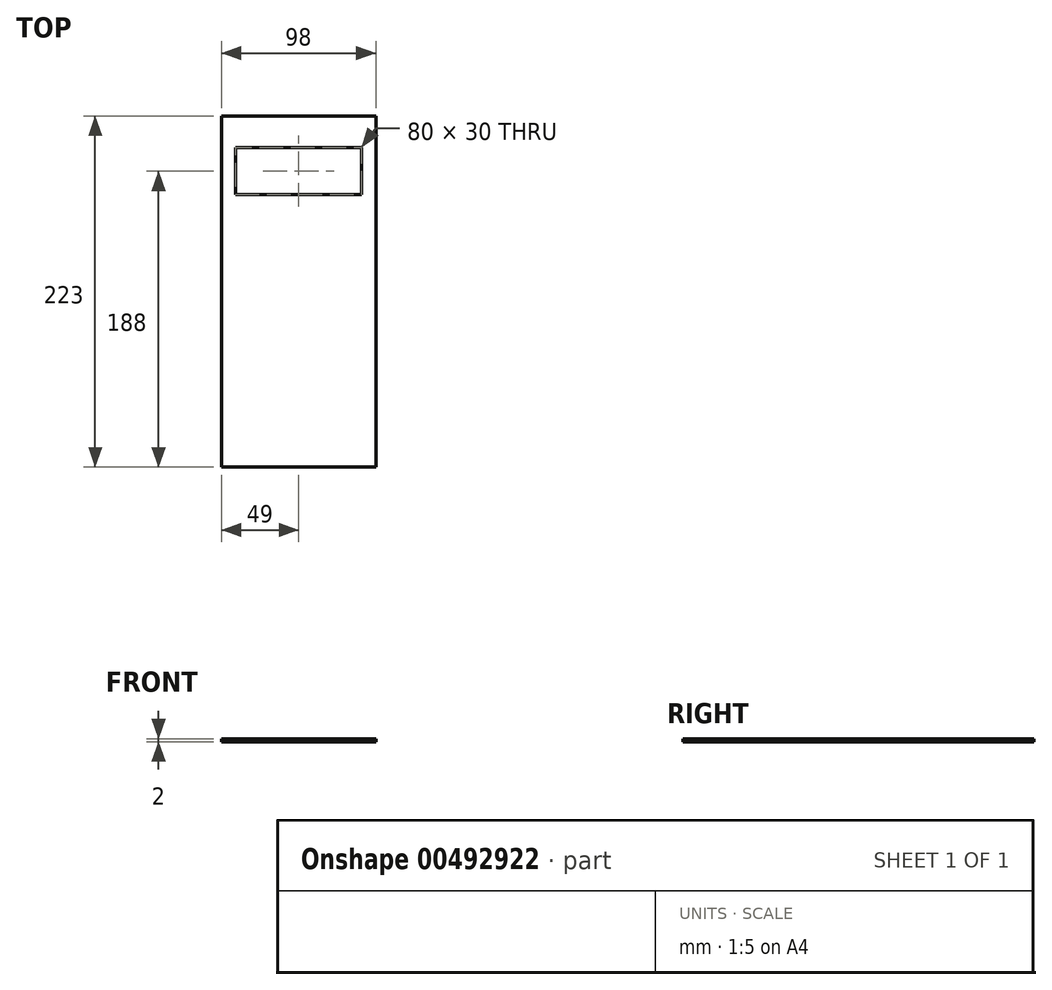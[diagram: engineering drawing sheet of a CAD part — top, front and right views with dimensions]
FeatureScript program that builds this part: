
annotation { "Feature Type Name" : "Feature", "Feature Type Description" : "" }
export const myFeature = defineFeature(function(context is Context, id is Id, definition is map)
    precondition{}
    {
        {
            var Q0;
            Q0=qCreatedBy(makeId("Top.planeOp"),FACE);
            var sketch = newSketch(context, id + "F0", { "sketchPlane" : qUnion([Q0])});
            skLineSegment(sketch, "E0.bottom", {"start": v(49, 111.5) * mm, "end": v(-49, 111.5) * mm});
            skLineSegment(sketch, "E0.top", {"start": v(49, -111.5) * mm, "end": v(-49, -111.5) * mm});
            skLineSegment(sketch, "E0.left", {"start": v(49, 111.5) * mm, "end": v(49, -111.5) * mm});
            skLineSegment(sketch, "E0.right", {"start": v(-49, 111.5) * mm, "end": v(-49, -111.5) * mm});
            skPoint(sketch, "E0.middle", {"position": v(0, 0) * mm});
            skLineSegment(sketch, "E1.bottom", {"start": v(40, 61.5) * mm, "end": v(-40, 61.5) * mm});
            skLineSegment(sketch, "E1.top", {"start": v(40, 91.5) * mm, "end": v(-40, 91.5) * mm});
            skLineSegment(sketch, "E1.left", {"start": v(40, 61.5) * mm, "end": v(40, 91.5) * mm});
            skLineSegment(sketch, "E1.right", {"start": v(-40, 61.5) * mm, "end": v(-40, 91.5) * mm});
            skPoint(sketch, "E1.middle", {"position": v(0, 76.5) * mm});
            skSolve(sketch);
        }
        {
            var Q0;
            Q0=makeQuery(id+"F0.imprint","IMPRINT",FACE,{"disambiguationData":[TD([[makeQuery(id+"F0.imprint","IMPRINT",EDGE,{"derivedFrom":sQuery(id+"F0.wireOp",EDGE,"E0.bottom")}),1.0]])]});
            extrude(context, id + "F1", {"entities" : qUnion([Q0]), "depth" : 2 * mm, "offsetDistance" : 25 * mm});
        }
    });
